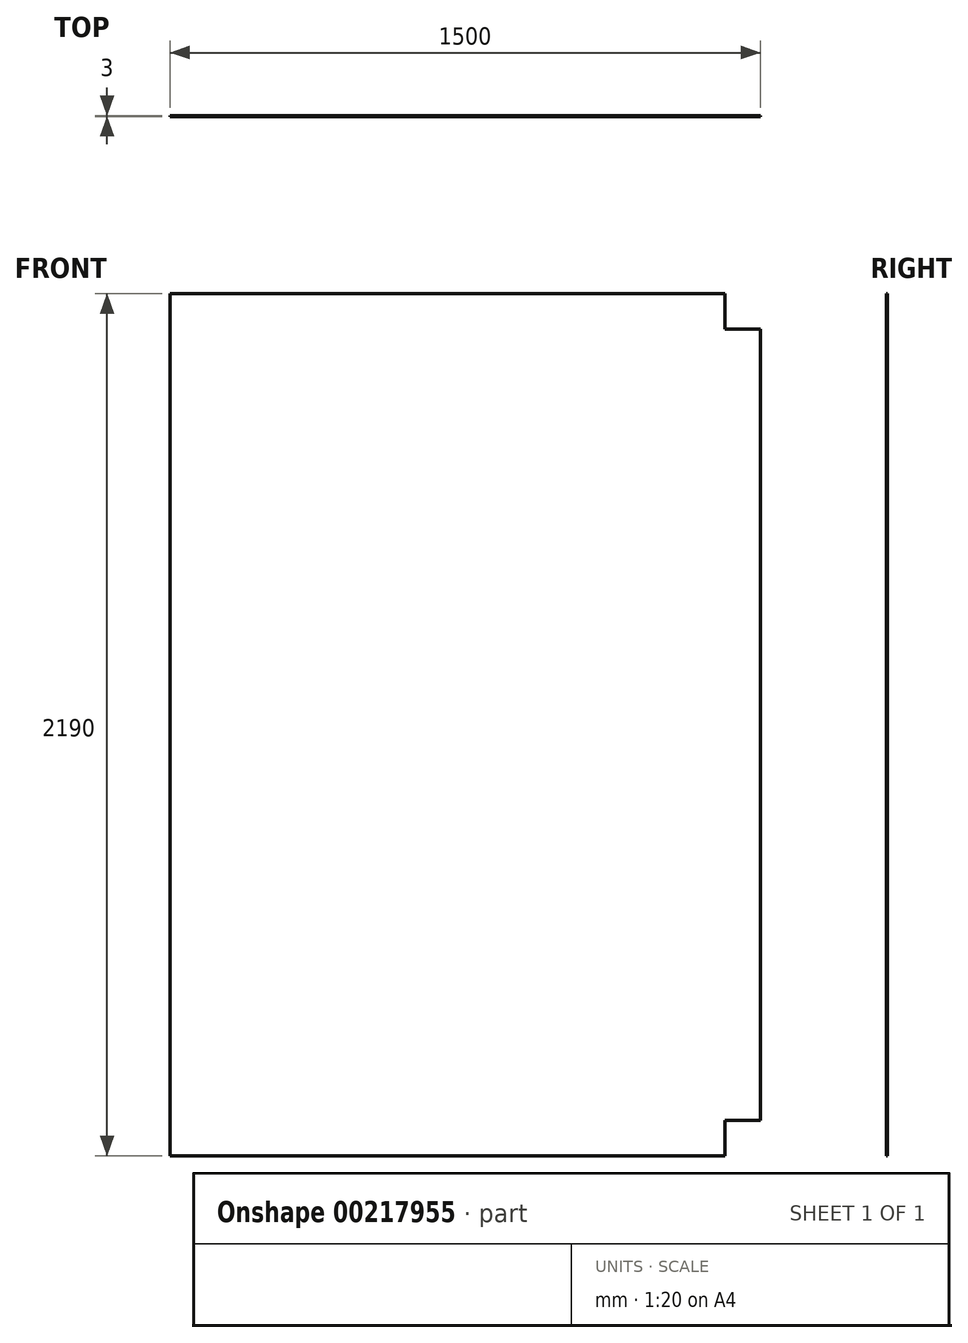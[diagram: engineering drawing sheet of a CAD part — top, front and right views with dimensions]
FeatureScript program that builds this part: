
annotation { "Feature Type Name" : "Feature", "Feature Type Description" : "" }
export const myFeature = defineFeature(function(context is Context, id is Id, definition is map)
    precondition{}
    {
        {
            var Q0;
            Q0=qCreatedBy(makeId("Front.planeOp"),FACE);
            var sketch = newSketch(context, id + "F0", { "sketchPlane" : qUnion([Q0])});
            skLineSegment(sketch, "E0.bottom", {"start": v(0, 0) * mm, "end": v(1410, 0) * mm});
            skLineSegment(sketch, "E0.top", {"start": v(0, -2010) * mm, "end": v(1410, -2010) * mm});
            skLineSegment(sketch, "E0.left", {"start": v(0, 0) * mm, "end": v(0, -2010) * mm});
            skLineSegment(sketch, "E0.right", {"start": v(1410, 0) * mm, "end": v(1410, -2010) * mm});
            skLineSegment(sketch, "E1.top", {"start": v(0, 90) * mm, "end": v(1410, 90) * mm});
            skLineSegment(sketch, "E1.left", {"start": v(0, 0) * mm, "end": v(0, 90) * mm});
            skLineSegment(sketch, "E1.right", {"start": v(1410, 0) * mm, "end": v(1410, 90) * mm});
            skLineSegment(sketch, "E2.bottom", {"start": v(1410, 0) * mm, "end": v(1500, 0) * mm});
            skLineSegment(sketch, "E2.top", {"start": v(1410, -2010) * mm, "end": v(1500, -2010) * mm});
            skLineSegment(sketch, "E2.right", {"start": v(1500, 0) * mm, "end": v(1500, -2010) * mm});
            skLineSegment(sketch, "E3.top", {"start": v(0, -2100) * mm, "end": v(1410, -2100) * mm});
            skLineSegment(sketch, "E3.left", {"start": v(0, -2010) * mm, "end": v(0, -2100) * mm});
            skLineSegment(sketch, "E3.right", {"start": v(1410, -2010) * mm, "end": v(1410, -2100) * mm});
            skSolve(sketch);
        }
        {
            var Q0;
            Q0=makeQuery(id+"F0.imprint","IMPRINT",FACE,{"disambiguationData":[TD([[makeQuery(id+"F0.imprint","IMPRINT",EDGE,{"derivedFrom":sQuery(id+"F0.wireOp",EDGE,"E0.left")}),1.0]])]});
            var Q1;
            Q1=makeQuery(id+"F0.imprint","IMPRINT",FACE,{"disambiguationData":[TD([[makeQuery(id+"F0.imprint","IMPRINT",EDGE,{"derivedFrom":sQuery(id+"F0.wireOp",EDGE,"E0.bottom")}),1.0]])]});
            var Q2;
            Q2=makeQuery(id+"F0.imprint","IMPRINT",FACE,{"disambiguationData":[TD([[makeQuery(id+"F0.imprint","IMPRINT",EDGE,{"derivedFrom":sQuery(id+"F0.wireOp",EDGE,"E2.bottom")}),-1.0]])]});
            var Q3;
            Q3=makeQuery(id+"F0.imprint","IMPRINT",FACE,{"disambiguationData":[TD([[makeQuery(id+"F0.imprint","IMPRINT",EDGE,{"derivedFrom":sQuery(id+"F0.wireOp",EDGE,"E0.top")}),-1.0]])]});
            extrude(context, id + "F1", {"entities" : qUnion([Q0, Q1, Q2, Q3]), "depth" : 3 * mm});
        }
    });
